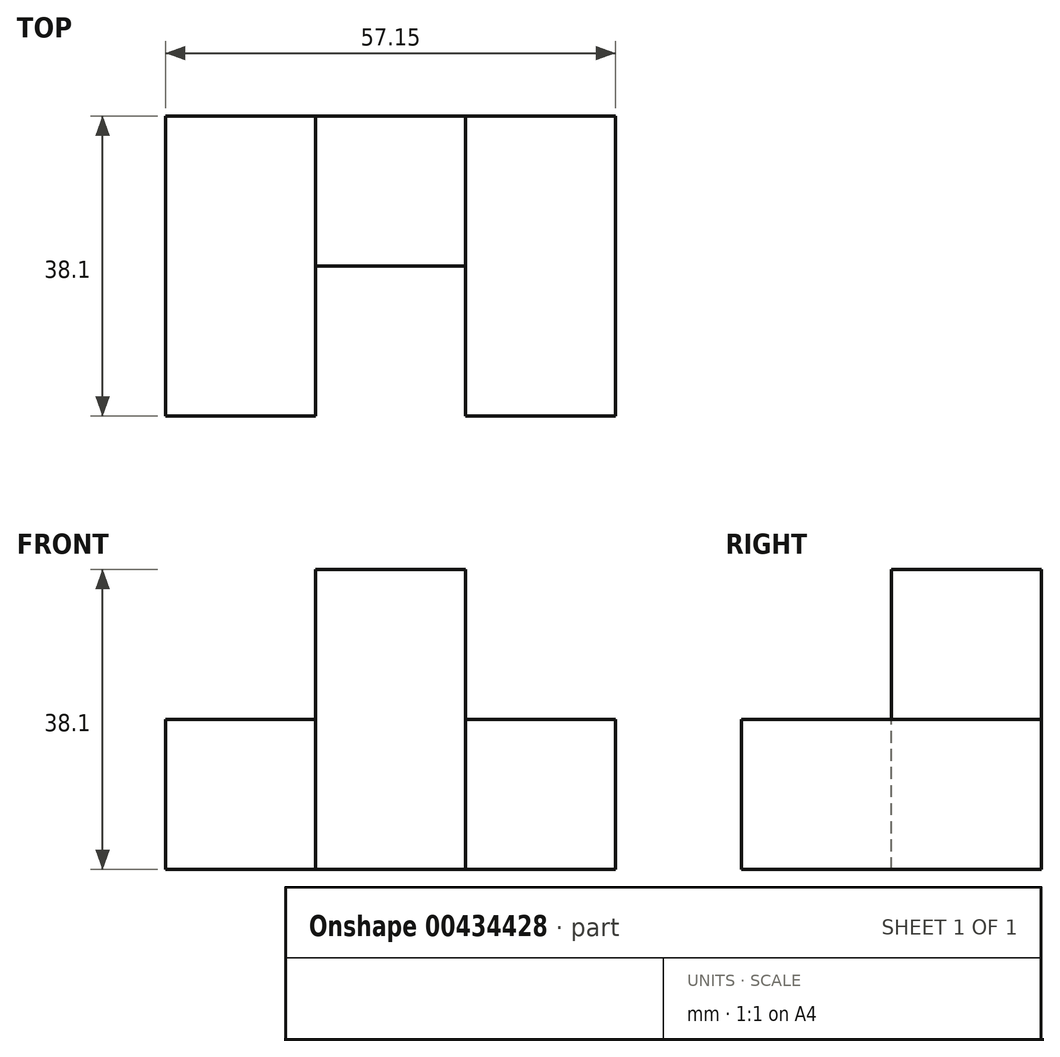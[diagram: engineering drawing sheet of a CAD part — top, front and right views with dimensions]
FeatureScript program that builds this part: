
annotation { "Feature Type Name" : "Feature", "Feature Type Description" : "" }
export const myFeature = defineFeature(function(context is Context, id is Id, definition is map)
    precondition{}
    {
        {
            var Q0;
            Q0=qCreatedBy(makeId("Front.planeOp"),FACE);
            var sketch = newSketch(context, id + "F0", { "sketchPlane" : qUnion([Q0])});
            skLineSegment(sketch, "E0", {"start": v(-41.59, 42.23) * mm, "end": v(-41.59, -45.94) * mm});
            skLineSegment(sketch, "E1", {"start": v(-41.59, -45.94) * mm, "end": v(48.14, -45.94) * mm});
            skLineSegment(sketch, "E2", {"start": v(48.14, -45.94) * mm, "end": v(48.14, 42.23) * mm});
            skLineSegment(sketch, "E3", {"start": v(48.14, 42.23) * mm, "end": v(-41.59, 42.23) * mm});
            skLineSegment(sketch, "E4", {"start": v(-27.31, -38.1) * mm, "end": v(29.84, -38.1) * mm});
            skLineSegment(sketch, "E5", {"start": v(29.84, -38.1) * mm, "end": v(29.84, -19.05) * mm});
            skLineSegment(sketch, "E6", {"start": v(29.84, -19.05) * mm, "end": v(10.79, -19.05) * mm});
            skLineSegment(sketch, "E7", {"start": v(-27.31, -38.1) * mm, "end": v(-27.31, -19.05) * mm});
            skLineSegment(sketch, "E8", {"start": v(-27.31, -19.05) * mm, "end": v(-8.26, -19.05) * mm});
            skLineSegment(sketch, "E9", {"start": v(-8.26, -19.05) * mm, "end": v(-8.26, 0) * mm});
            skLineSegment(sketch, "E10", {"start": v(-8.26, 0) * mm, "end": v(10.79, 0) * mm});
            skLineSegment(sketch, "E11", {"start": v(10.79, 0) * mm, "end": v(10.79, -19.05) * mm});
            skLineSegment(sketch, "E12", {"start": v(-8.26, -19.05) * mm, "end": v(10.79, -19.05) * mm});
            skLineSegment(sketch, "E13", {"start": v(-8.26, -19.05) * mm, "end": v(-8.26, -38.1) * mm});
            skLineSegment(sketch, "E14", {"start": v(-8.26, -38.1) * mm, "end": v(10.79, -38.1) * mm});
            skLineSegment(sketch, "E15", {"start": v(10.79, -38.1) * mm, "end": v(10.79, -19.05) * mm});
            skSolve(sketch);
        }
        {
            var Q0;
            {var subQ0=sQuery(id+"F0.wireOp",EDGE,"E7");Q0=makeQuery(id+"F0.imprint","IMPRINT",FACE,{"disambiguationData":[TD([[makeQuery(id+"F0.imprint","IMPRINT",EDGE,{"derivedFrom":subQ0}),-1.0]])]});}
            var Q1;
            {var subQ0=sQuery(id+"F0.wireOp",EDGE,"E5");Q1=makeQuery(id+"F0.imprint","IMPRINT",FACE,{"disambiguationData":[TD([[makeQuery(id+"F0.imprint","IMPRINT",EDGE,{"derivedFrom":subQ0}),1.0]])]});}
            extrude(context, id + "F1", {"entities" : qUnion([Q0, Q1]), "depth" : 38.1 * mm});
        }
        {
            var Q0;
            Q0=makeQuery(id+"F0.imprint","IMPRINT",FACE,{"disambiguationData":[TD([[makeQuery(id+"F0.imprint","IMPRINT",EDGE,{"derivedFrom":sQuery(id+"F0.wireOp",EDGE,"E12")}),-1.0]])]});
            var Q1;
            Q1=makeQuery(id+"F0.imprint","IMPRINT",FACE,{"disambiguationData":[TD([[makeQuery(id+"F0.imprint","IMPRINT",EDGE,{"derivedFrom":sQuery(id+"F0.wireOp",EDGE,"E9")}),-1.0]])]});
            extrude(context, id + "F2", {"entities" : qUnion([Q0, Q1]), "depth" : 19.05 * mm});
        }
    });
